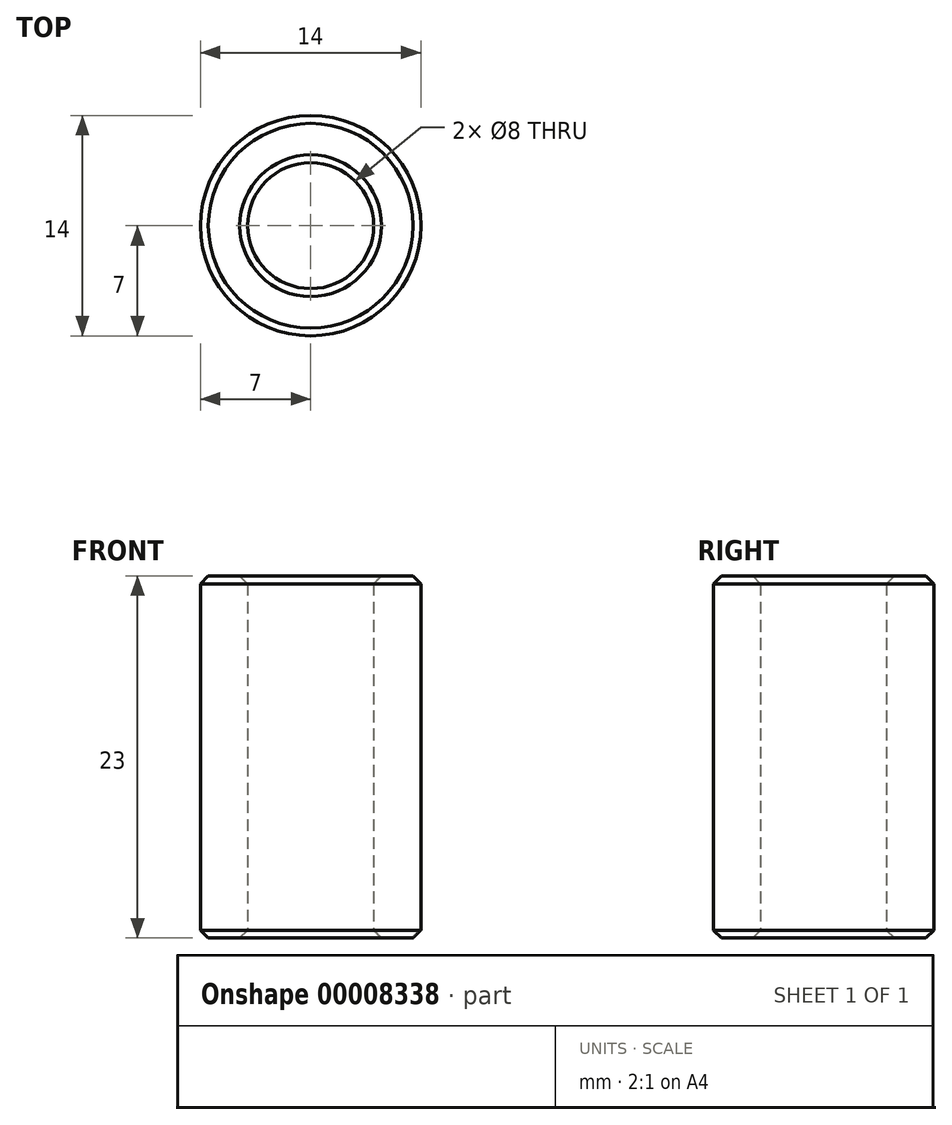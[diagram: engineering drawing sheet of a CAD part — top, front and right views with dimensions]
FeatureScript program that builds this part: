
annotation { "Feature Type Name" : "Feature", "Feature Type Description" : "" }
export const myFeature = defineFeature(function(context is Context, id is Id, definition is map)
    precondition{}
    {
        {
            var Q0;
            Q0=qCreatedBy(makeId("Top.planeOp"),FACE);
            var sketch = newSketch(context, id + "F0", { "sketchPlane" : qUnion([Q0])});
            skCircle(sketch, "E0", {"center": v(0, 0) * mm, "radius": 4 * mm});
            skCircle(sketch, "E1", {"center": v(0, 0) * mm, "radius": 7 * mm});
            skSolve(sketch);
        }
        {
            var Q0;
            Q0 = qSketchRegion(id + "F0", true);
            extrude(context, id + "F1", {"entities" : qUnion([Q0]), "depth" : 23 * mm});
        }
        {
            var Q0;
            Q0=makeQuery(id+"F1.opExtrude","CAP_EDGE",EDGE,{"disambiguationData":[OSD([sQuery(id+"F0.wireOp",EDGE,"E0")])],"isStart":false});
            var Q1;
            Q1=makeQuery(id+"F1.opExtrude","CAP_EDGE",EDGE,{"disambiguationData":[OSD([sQuery(id+"F0.wireOp",EDGE,"E1")])],"isStart":false});
            var Q2;
            Q2=makeQuery(id+"F1.opExtrude","CAP_EDGE",EDGE,{"disambiguationData":[OSD([sQuery(id+"F0.wireOp",EDGE,"E0")])],"isStart":true});
            var Q3;
            Q3=makeQuery(id+"F1.opExtrude","CAP_EDGE",EDGE,{"disambiguationData":[OSD([sQuery(id+"F0.wireOp",EDGE,"E1")])],"isStart":true});
            chamfer(context, id + "F2", {"entities" : qUnion([Q0, Q1, Q2, Q3]), "width" : 0.5 * mm, "tangentPropagation" : true});
        }
    });
